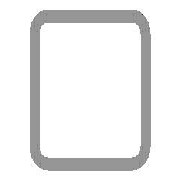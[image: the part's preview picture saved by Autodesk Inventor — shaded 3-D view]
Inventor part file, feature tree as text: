
AUTODESK INVENTOR PART (.ipt)
format: ipt  version: 2025.1 (Build 291241020, 241B)  size: 134,144 bytes
history: native  units: mm (DEFAULTED — no unit token found)
features: other x4, sketch x1, plane x1
ambient origin geometry x8: Origin, YZ Plane, XZ Plane, XY Plane, X Axis, Y Axis, Z Axis, Center Point
bodies: Solid1 (feature_tree), Body (feature_tree)
feature tree (6):
  parser-record x1  (decoder bookkeeping rows leaked as tree rows — omitted from the tree; the rows remain in map.json)
  other  "Driven Length"
  other  "Start Plane"
  other  "End Plane"
  sketch  "Sketch3"  dims[d3=3400.0mm d4=0.0mm d7=6.0mm d9=80.0mm d11=80.0mm d12=3.0mm d13=-0.0mm d14=3400.0mm d15=40.0mm d16=40.0mm d17=90.0deg d18=3400.0mm]
  plane  "Work Plane3"
